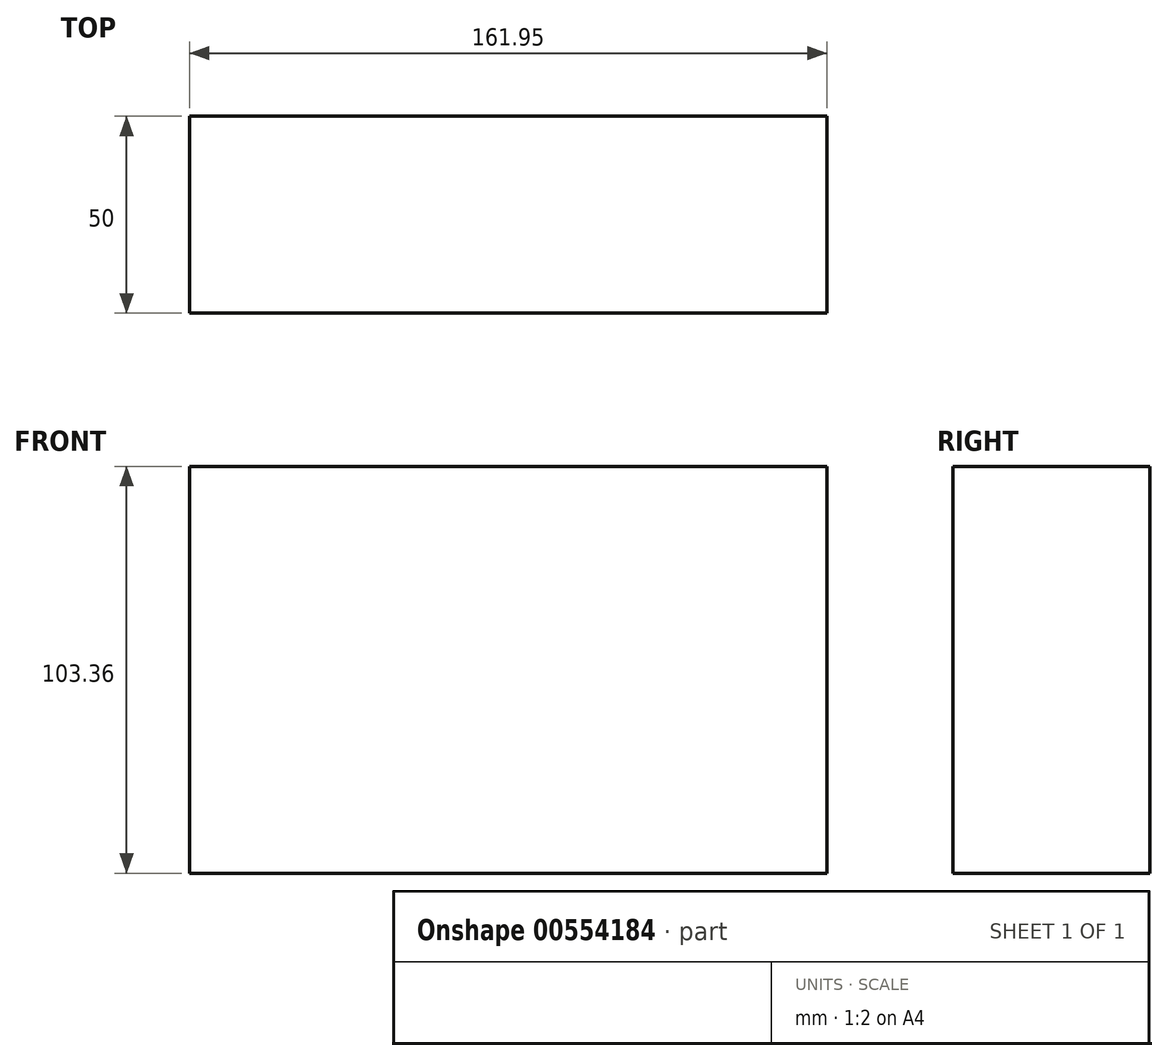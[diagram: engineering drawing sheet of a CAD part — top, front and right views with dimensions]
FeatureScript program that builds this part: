
annotation { "Feature Type Name" : "Feature", "Feature Type Description" : "" }
export const myFeature = defineFeature(function(context is Context, id is Id, definition is map)
    precondition{}
    {
        {
            var Q0;
            Q0=qCreatedBy(makeId("Front.planeOp"),FACE);
            var sketch = newSketch(context, id + "F0", { "sketchPlane" : qUnion([Q0])});
            skLineSegment(sketch, "E0.bottom", {"start": v(-122.67, 45.83) * mm, "end": v(39.28, 45.83) * mm});
            skLineSegment(sketch, "E0.top", {"start": v(-122.67, -57.53) * mm, "end": v(39.28, -57.53) * mm});
            skLineSegment(sketch, "E0.left", {"start": v(-122.67, 45.83) * mm, "end": v(-122.67, -57.53) * mm});
            skLineSegment(sketch, "E0.right", {"start": v(39.28, 45.83) * mm, "end": v(39.28, -57.53) * mm});
            skSolve(sketch);
        }
        {
            var Q0;
            Q0=makeQuery(id+"F0.imprint","IMPRINT",FACE,{"disambiguationData":[TD([[makeQuery(id+"F0.imprint","IMPRINT",EDGE,{"derivedFrom":sQuery(id+"F0.wireOp",EDGE,"E0.bottom")}),-1.0]])]});
            extrude(context, id + "F1", {"entities" : qUnion([Q0]), "depth" : 50 * mm, "offsetDistance" : 25.4 * mm});
        }
    });
